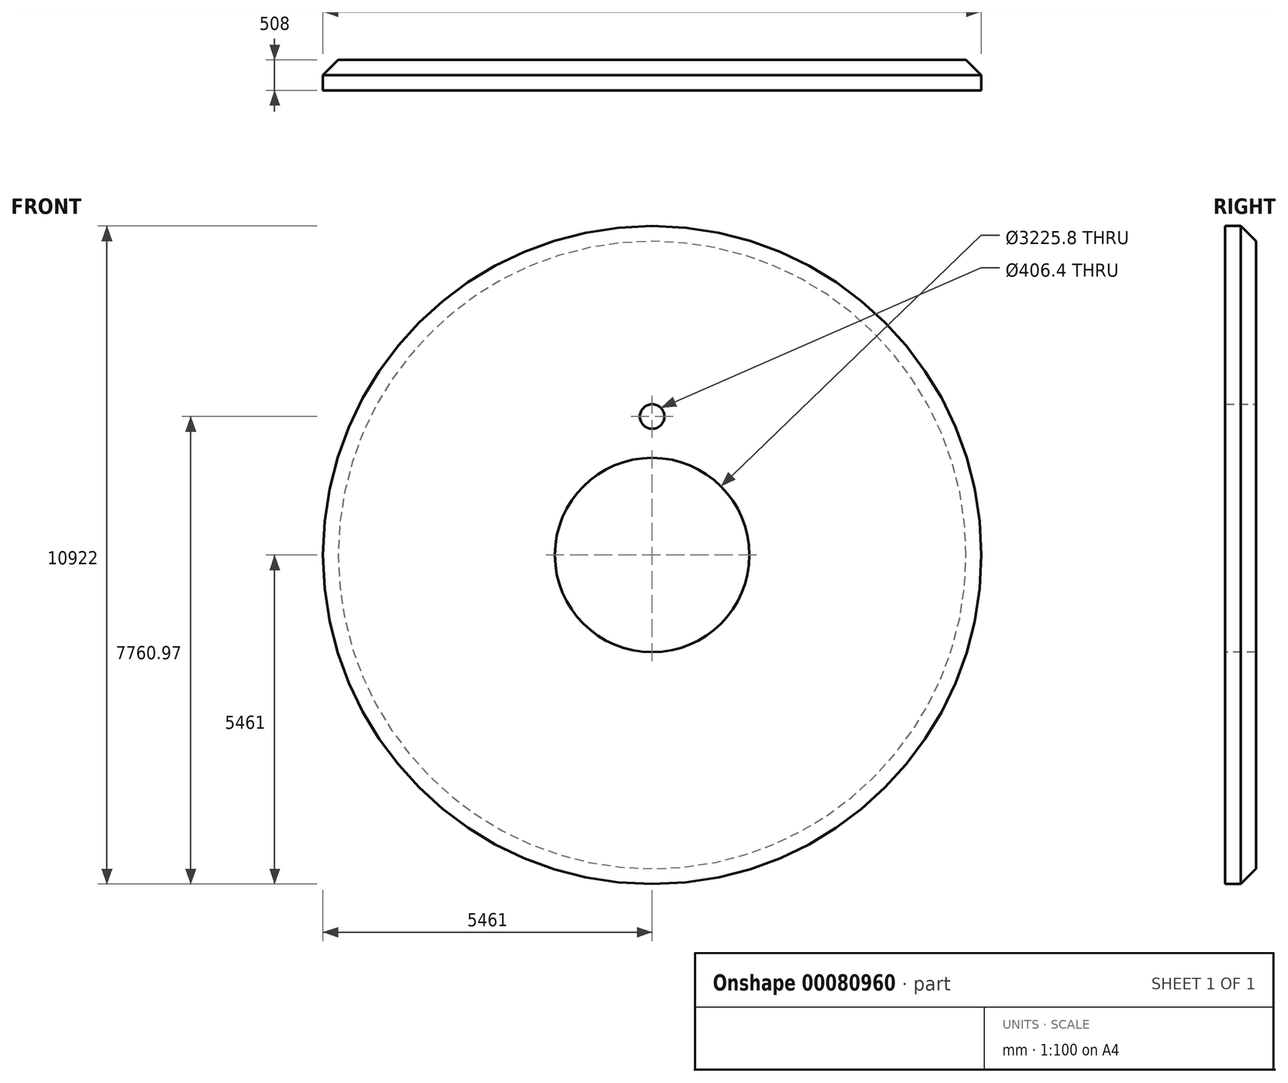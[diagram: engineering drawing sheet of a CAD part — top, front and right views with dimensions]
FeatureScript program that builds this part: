
annotation { "Feature Type Name" : "Feature", "Feature Type Description" : "" }
export const myFeature = defineFeature(function(context is Context, id is Id, definition is map)
    precondition{}
    {
        {
            var Q0;
            Q0=qCreatedBy(makeId("Right.planeOp"),FACE);
            var sketch = newSketch(context, id + "F0", { "sketchPlane" : qUnion([Q0])});
            skLineSegment(sketch, "E0.bottom", {"start": v(0, 1612.9) * mm, "end": v(508, 1612.9) * mm});
            skLineSegment(sketch, "E0.top", {"start": v(0, 5461) * mm, "end": v(508, 5461) * mm});
            skLineSegment(sketch, "E0.left", {"start": v(0, 1612.9) * mm, "end": v(0, 5461) * mm});
            skLineSegment(sketch, "E0.right", {"start": v(508, 1612.9) * mm, "end": v(508, 5461) * mm});
            skLineSegment(sketch, "E1", {"start": v(0, 0) * mm, "end": v(698.55, 0) * mm});
            skSolve(sketch);
        }
        {
            var Q0;
            Q0=makeQuery(id+"F0.imprint","IMPRINT",FACE,{"disambiguationData":[TD([[makeQuery(id+"F0.imprint","IMPRINT",EDGE,{"derivedFrom":sQuery(id+"F0.wireOp",EDGE,"E0.bottom")}),1.0]])]});
            var Q1;
            Q1=sQuery(id+"F0.wireOp",EDGE,"E1");
            revolve(context, id + "F1", {"entities" : qUnion([Q0]), "axis" : qUnion([Q1]), "revolveType" : RevolveType.FULL});
        }
        {
            var Q0;
            Q0=makeQuery(id+"F1.opRevolve","SWEPT_EDGE",EDGE,{"disambiguationData":[OSD([sQuery(id+"F0.wireOp",EDGE,"E0.top"),sQuery(id+"F0.wireOp",EDGE,"E0.right")])]});
            chamfer(context, id + "F2", {"entities" : qUnion([Q0]), "width" : 254 * mm, "tangentPropagation" : true});
        }
        {
            var Q0;
            Q0=makeQuery(id+"F1.opRevolve","SWEPT_FACE",FACE,{"disambiguationData":[OSD([sQuery(id+"F0.wireOp",EDGE,"E0.right")])]});
            var sketch = newSketch(context, id + "F3", { "sketchPlane" : qUnion([Q0])});
            skCircle(sketch, "E2", {"center": v(0, 2299.97) * mm, "radius": 203.2 * mm});
            skSolve(sketch);
        }
        {
            var Q0;
            Q0 = qSketchRegion(id + "F3", true);
            extrude(context, id + "F4", {"entities" : qUnion([Q0]), "operationType" : NewBodyOperationType.REMOVE, "endBound" : BoundingType.THROUGH_ALL, "oppositeDirection" : true, "depth" : 25.4 * mm});
        }
    });
